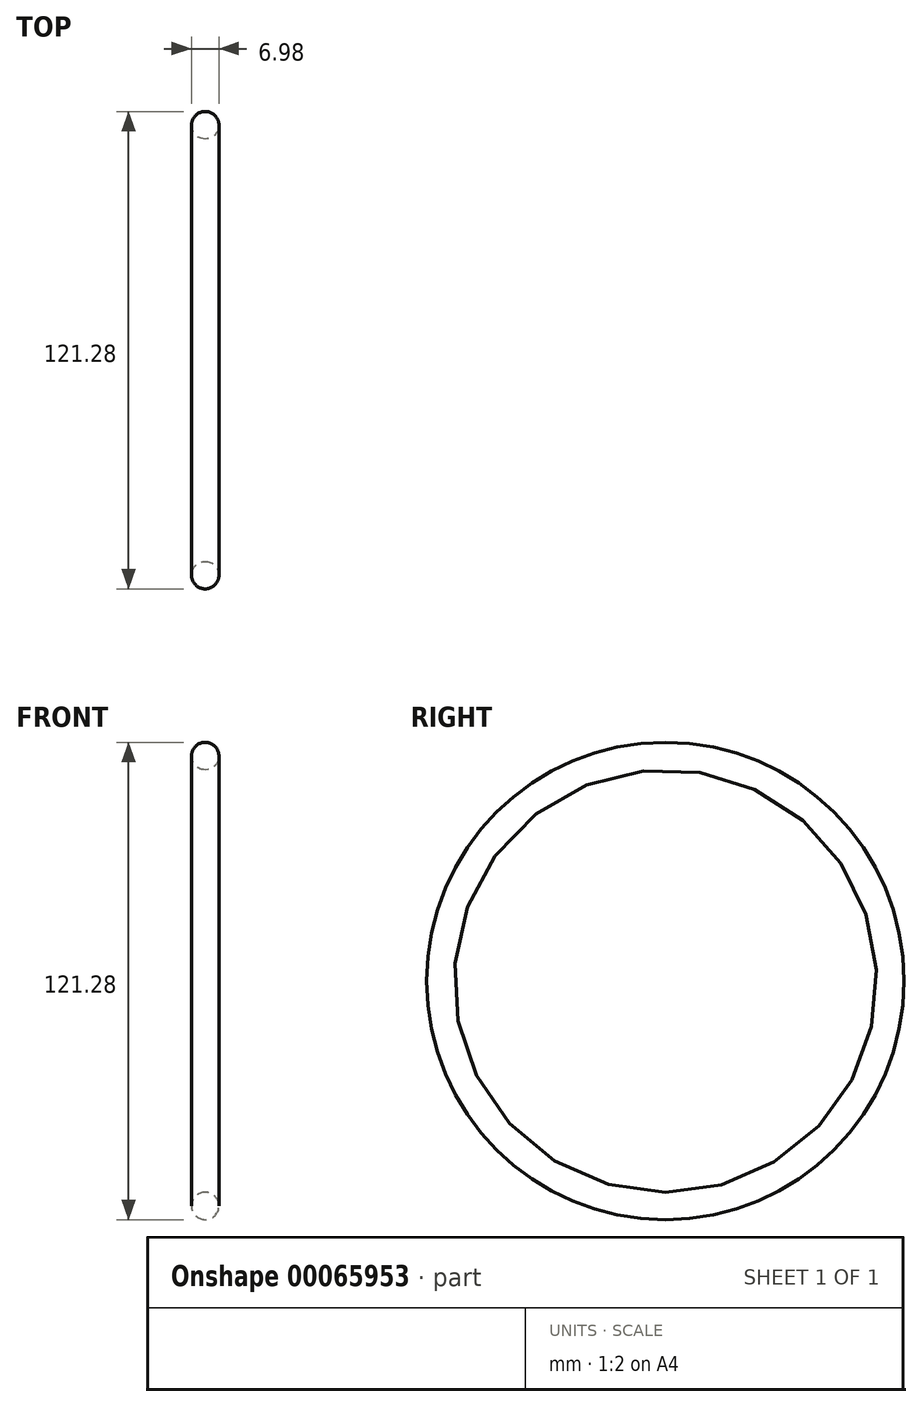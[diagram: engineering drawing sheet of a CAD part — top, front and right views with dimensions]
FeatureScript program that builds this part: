
annotation { "Feature Type Name" : "Feature", "Feature Type Description" : "" }
export const myFeature = defineFeature(function(context is Context, id is Id, definition is map)
    precondition{}
    {
        {
            var Q0;
            Q0=qCreatedBy(makeId("Front.planeOp"),FACE);
            var sketch = newSketch(context, id + "F0", { "sketchPlane" : qUnion([Q0])});
            skLineSegment(sketch, "E0", {"start": v(0, 0) * mm, "end": v(-6.06, 0) * mm, "construction": true});
            skCircle(sketch, "E1", {"center": v(0, 57.15) * mm, "radius": 3.5 * mm});
            skSolve(sketch);
        }
        {
            var Q0;
            Q0=makeQuery(id+"F0.imprint","IMPRINT",FACE,{"disambiguationData":[TD([[makeQuery(id+"F0.imprint","IMPRINT",EDGE,{"derivedFrom":sQuery(id+"F0.wireOp",EDGE,"E1")}),1.0]])]});
            var Q1;
            Q1=sQuery(id+"F0.wireOp",EDGE,"E0");
            revolve(context, id + "F1", {"entities" : qUnion([Q0]), "axis" : qUnion([Q1]), "revolveType" : RevolveType.FULL});
        }
    });
